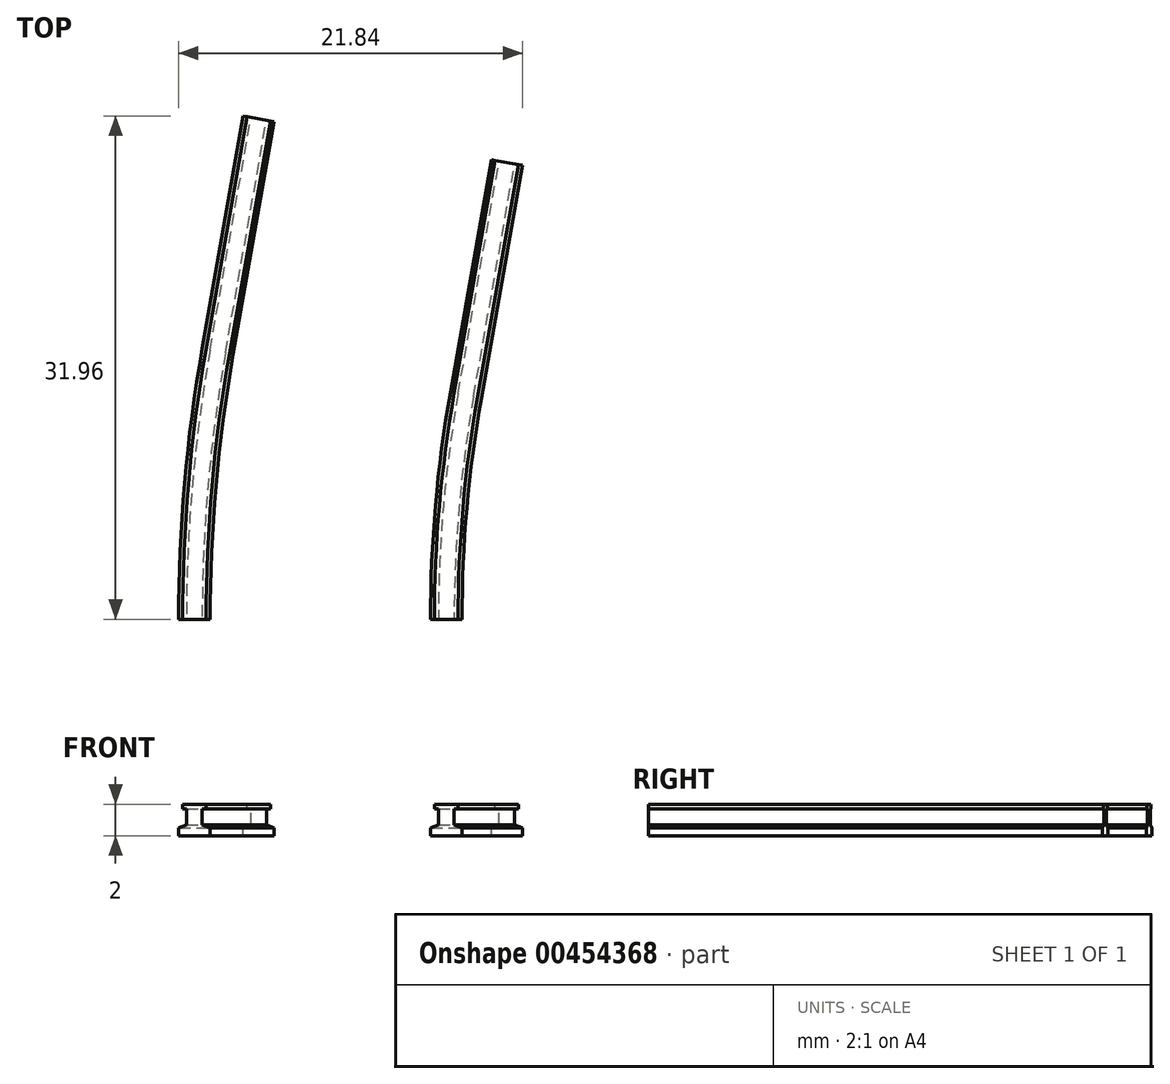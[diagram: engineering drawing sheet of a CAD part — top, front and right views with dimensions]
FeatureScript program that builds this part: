
annotation { "Feature Type Name" : "Feature", "Feature Type Description" : "" }
export const myFeature = defineFeature(function(context is Context, id is Id, definition is map)
    precondition{}
    {
        {
            var Q0;
            Q0=qCreatedBy(makeId("Top.planeOp"),FACE);
            var sketch = newSketch(context, id + "F0", { "sketchPlane" : qUnion([Q0])});
            skArc(sketch, "E0", {"start": v(1.37, 15.63) * mm, "mid": v(0.34, 7.84) * mm, "end": v(0, 0) * mm});
            skLineSegment(sketch, "E1", {"start": v(0, 0) * mm, "end": v(90, 0) * mm, "construction": true});
            skLineSegment(sketch, "E2", {"start": v(1.37, 15.63) * mm, "end": v(90, 0) * mm, "construction": true});
            skLineSegment(sketch, "E3", {"start": v(1.37, 15.63) * mm, "end": v(3.97, 30.4) * mm});
            skSolve(sketch);
        }
        {
            var Q0;
            Q0=qCreatedBy(makeId("Front.planeOp"),FACE);
            var sketch = newSketch(context, id + "F1", { "sketchPlane" : qUnion([Q0])});
            skLineSegment(sketch, "E4", {"start": v(0, 4.7) * mm, "end": v(0, 0) * mm, "construction": true});
            skLineSegment(sketch, "E5", {"start": v(-8, 0) * mm, "end": v(-8, 4.6) * mm, "construction": true});
            skLineSegment(sketch, "E6", {"start": v(-8, 0) * mm, "end": v(-9, 0) * mm});
            skLineSegment(sketch, "E7", {"start": v(-9, 0) * mm, "end": v(-9, 0.5) * mm});
            skLineSegment(sketch, "E8", {"start": v(-9, 0.5) * mm, "end": v(-8.5, 0.7) * mm});
            skLineSegment(sketch, "E9", {"start": v(-8.5, 0.7) * mm, "end": v(-8.5, 1.7) * mm});
            skLineSegment(sketch, "E10", {"start": v(-8.5, 1.7) * mm, "end": v(-8.75, 1.7) * mm});
            skLineSegment(sketch, "E11", {"start": v(-8.75, 1.7) * mm, "end": v(-8.75, 2) * mm});
            skLineSegment(sketch, "E12", {"start": v(-8.75, 2) * mm, "end": v(-8, 2) * mm});
            skLineSegment(sketch, "E13.MirrorCS", {"start": v(-7.25, 2) * mm, "end": v(-8, 2) * mm});
            skLineSegment(sketch, "E14.MirrorCS", {"start": v(-7.25, 1.7) * mm, "end": v(-7.25, 2) * mm});
            skLineSegment(sketch, "E15.MirrorCS", {"start": v(-7.5, 1.7) * mm, "end": v(-7.25, 1.7) * mm});
            skLineSegment(sketch, "E16.MirrorCS", {"start": v(-7.5, 0.7) * mm, "end": v(-7.5, 1.7) * mm});
            skLineSegment(sketch, "E17.MirrorCS", {"start": v(-7, 0.5) * mm, "end": v(-7.5, 0.7) * mm});
            skLineSegment(sketch, "E18.MirrorCS", {"start": v(-7, 0) * mm, "end": v(-7, 0.5) * mm});
            skLineSegment(sketch, "E19.MirrorCS", {"start": v(-8, 0) * mm, "end": v(-7, 0) * mm});
            skLineSegment(sketch, "E20.MirrorCS", {"start": v(9, 0) * mm, "end": v(9, 0.5) * mm});
            skLineSegment(sketch, "E21.MirrorCS", {"start": v(8, 0) * mm, "end": v(9, 0) * mm});
            skLineSegment(sketch, "E22.MirrorCS", {"start": v(8, 0) * mm, "end": v(7, 0) * mm});
            skLineSegment(sketch, "E23.MirrorCS", {"start": v(7, 0) * mm, "end": v(7, 0.5) * mm});
            skLineSegment(sketch, "E24.MirrorCS", {"start": v(7, 0.5) * mm, "end": v(7.5, 0.7) * mm});
            skLineSegment(sketch, "E25.MirrorCS", {"start": v(7.5, 0.7) * mm, "end": v(7.5, 1.7) * mm});
            skLineSegment(sketch, "E26.MirrorCS", {"start": v(7.5, 1.7) * mm, "end": v(7.25, 1.7) * mm});
            skLineSegment(sketch, "E27.MirrorCS", {"start": v(7.25, 1.7) * mm, "end": v(7.25, 2) * mm});
            skLineSegment(sketch, "E28.MirrorCS", {"start": v(7.25, 2) * mm, "end": v(8, 2) * mm});
            skLineSegment(sketch, "E29.MirrorCS", {"start": v(8.5, 1.7) * mm, "end": v(8.75, 1.7) * mm});
            skLineSegment(sketch, "E30.MirrorCS", {"start": v(8.75, 1.7) * mm, "end": v(8.75, 2) * mm});
            skLineSegment(sketch, "E31.MirrorCS", {"start": v(9, 0.5) * mm, "end": v(8.5, 0.7) * mm});
            skLineSegment(sketch, "E32.MirrorCS", {"start": v(8.5, 0.7) * mm, "end": v(8.5, 1.7) * mm});
            skLineSegment(sketch, "E33.MirrorCS", {"start": v(8.75, 2) * mm, "end": v(8, 2) * mm});
            skSolve(sketch);
        }
        {
            var Q0;
            Q0=makeQuery(id+"F1.imprint","IMPRINT",FACE,{"disambiguationData":[TD([[makeQuery(id+"F1.imprint","IMPRINT",EDGE,{"derivedFrom":sQuery(id+"F1.wireOp",EDGE,"E6")}),-1.0]])]});
            var Q1;
            Q1=makeQuery(id+"F1.imprint","IMPRINT",FACE,{"disambiguationData":[TD([[makeQuery(id+"F1.imprint","IMPRINT",EDGE,{"derivedFrom":sQuery(id+"F1.wireOp",EDGE,"E26.MirrorCS")}),-1.0]])]});
            var Q2;
            Q2=sQuery(id+"F0.wireOp",EDGE,"E0");
            var Q3;
            Q3=sQuery(id+"F0.wireOp",EDGE,"E3");
            sweep(context, id + "F2", {"profiles" : qUnion([Q0, Q1]), "path" : qUnion([Q2, Q3])});
        }
    });
